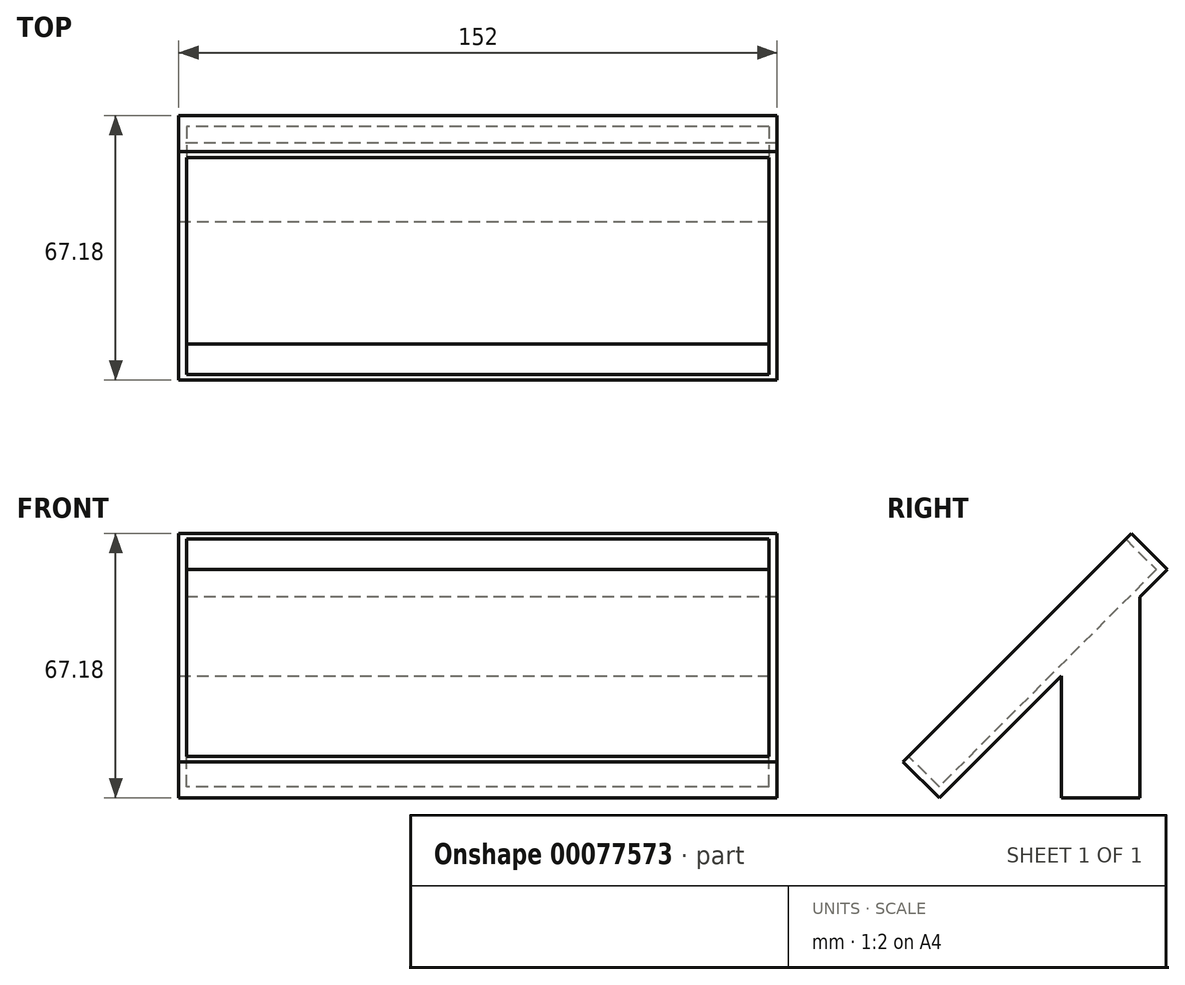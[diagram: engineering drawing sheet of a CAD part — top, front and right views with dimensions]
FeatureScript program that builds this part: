
annotation { "Feature Type Name" : "Feature", "Feature Type Description" : "" }
export const myFeature = defineFeature(function(context is Context, id is Id, definition is map)
    precondition{}
    {
        {
            var Q0;
            Q0=qCreatedBy(makeId("Right.planeOp"),FACE);
            var sketch = newSketch(context, id + "F0", { "sketchPlane" : qUnion([Q0])});
            skLineSegment(sketch, "E0", {"start": v(-33.59, -24.4) * mm, "end": v(24.4, 33.59) * mm});
            skLineSegment(sketch, "E1", {"start": v(24.4, 33.59) * mm, "end": v(33.59, 24.4) * mm});
            skLineSegment(sketch, "E2", {"start": v(33.59, 24.4) * mm, "end": v(-24.4, -33.59) * mm});
            skLineSegment(sketch, "E3", {"start": v(-24.4, -33.59) * mm, "end": v(-33.59, -24.4) * mm});
            skSolve(sketch);
        }
        {
            var Q0;
            Q0 = qSketchRegion(id + "F0", true);
            extrude(context, id + "F1", {"entities" : qUnion([Q0]), "depth" : 152 * mm});
        }
        {
            var Q0;
            Q0=makeQuery(id+"F1.opExtrude","SWEPT_FACE",FACE,{"disambiguationData":[OSD([sQuery(id+"F0.wireOp",EDGE,"E0")])]});
            shell(context, id + "F2", {"entities" : qUnion([Q0]), "thickness" : 2 * mm});
        }
        {
            var Q0;
            Q0=qCreatedBy(makeId("Right.planeOp"),FACE);
            var sketch = newSketch(context, id + "F3", { "sketchPlane" : qUnion([Q0])});
            skLineSegment(sketch, "E4", {"start": v(6.6, 0) * mm, "end": v(6.6, -33.59) * mm});
            skLineSegment(sketch, "E5", {"start": v(6.6, -33.59) * mm, "end": v(26.6, -33.59) * mm});
            skLineSegment(sketch, "E6", {"start": v(26.6, -33.59) * mm, "end": v(26.6, 0) * mm});
            skLineSegment(sketch, "E7", {"start": v(26.6, 0) * mm, "end": v(6.6, 0) * mm});
            skLineSegment(sketch, "E8", {"start": v(6.6, -33.59) * mm, "end": v(-24.4, -33.59) * mm, "construction": true});
            skLineSegment(sketch, "E9", {"start": v(26.6, 0) * mm, "end": v(26.6, 18.73) * mm});
            skLineSegment(sketch, "E10", {"start": v(26.6, 18.73) * mm, "end": v(8, 0) * mm});
            skSolve(sketch);
        }
        {
            var Q0;
            Q0 = qSketchRegion(id + "F3", true);
            extrude(context, id + "F4", {"entities" : qUnion([Q0]), "operationType" : NewBodyOperationType.ADD, "depth" : 152 * mm});
        }
    });
